# Revit family: QSC QIO-S4,IR1x4,GP8x8
name_source: partatom
category: Communication Devices
revit_build: Autodesk Revit 2018 (Build: 20190510_1515(x64)
units: mm (PartAtom-declared; Revit-internal decimal feet)

## family parameters
Cut with Voids When Loaded = No
Host = Face
Maintain Annotation Orientation = No
Part Type = Normal
Room Calculation Point = No
Round Connector Dimension = Use Diameter
Shared = No

## types (3) — shared parameters
Current Draw = 2.5
Depth = 139.7 mm  [stored 0.458333 ft]
Height = 40.4 mm
Manufacturer = QSC, LLC
Manufacturer URL = http://www.qsc.com
Mount Type = Surface or Rack
Mounting Width = 108 mm  [stored 0.354331 ft]
Product Documentation Link = https://www.qsc.com
Product Page URL = https://www.qsc.com
Rack Units = 1
Regulatory Compliance = FCC 47 CFR Part 15, IC ICES-003, CE (EN55032, EN55035), EU RoHS directive 2011/65/EU, WEEE directive 2012/19/EU, China RoHS directive GB/T26572, EAC, UL, C-UL, NOM-019
Temperature Max = 50° C
Temperature min = 0° C
URL = https://www.qsc.com
Voltage DC = 24 VDC, or PoE 802.3af Type 1
Weight Product (kg) = 0.54
Weight Product (lb) = 1.18
Width = 108 mm  [stored 0.354331 ft]
zero-valued in all types: Default Elevation

## per-type parameters (varying)
| type | Communication Ports | Description |
| QIO-S4 | 1 RS-232/485/422, 3 RS-232, LAN, LAN (THRU) | Network Serial I/O Expander for Q-SYS |
| QIO-IR1x4 | 4 IR/RS-232 (TX ONLY), 1 IR INPUT, LAN, LAN (THRU) | Network IR I/O Expander for Q-SYS |
| QIO-GP8x8 | 8 CONFIGURABLE GPI, 8 CONFIGURABLE GPO, LAN, LAN (THRU) | Network GPIO Expander for Q-SYS |

note: column(s) folded — value = type name in every type: Model

note: [stored X ft] marks values corroborated as IEEE doubles in the binary element streams (Revit-internal decimal feet)

## geometry (parser evidence)
native form markers: Blend x1, Sweep x2
no freeform markers — native parametric forms only
